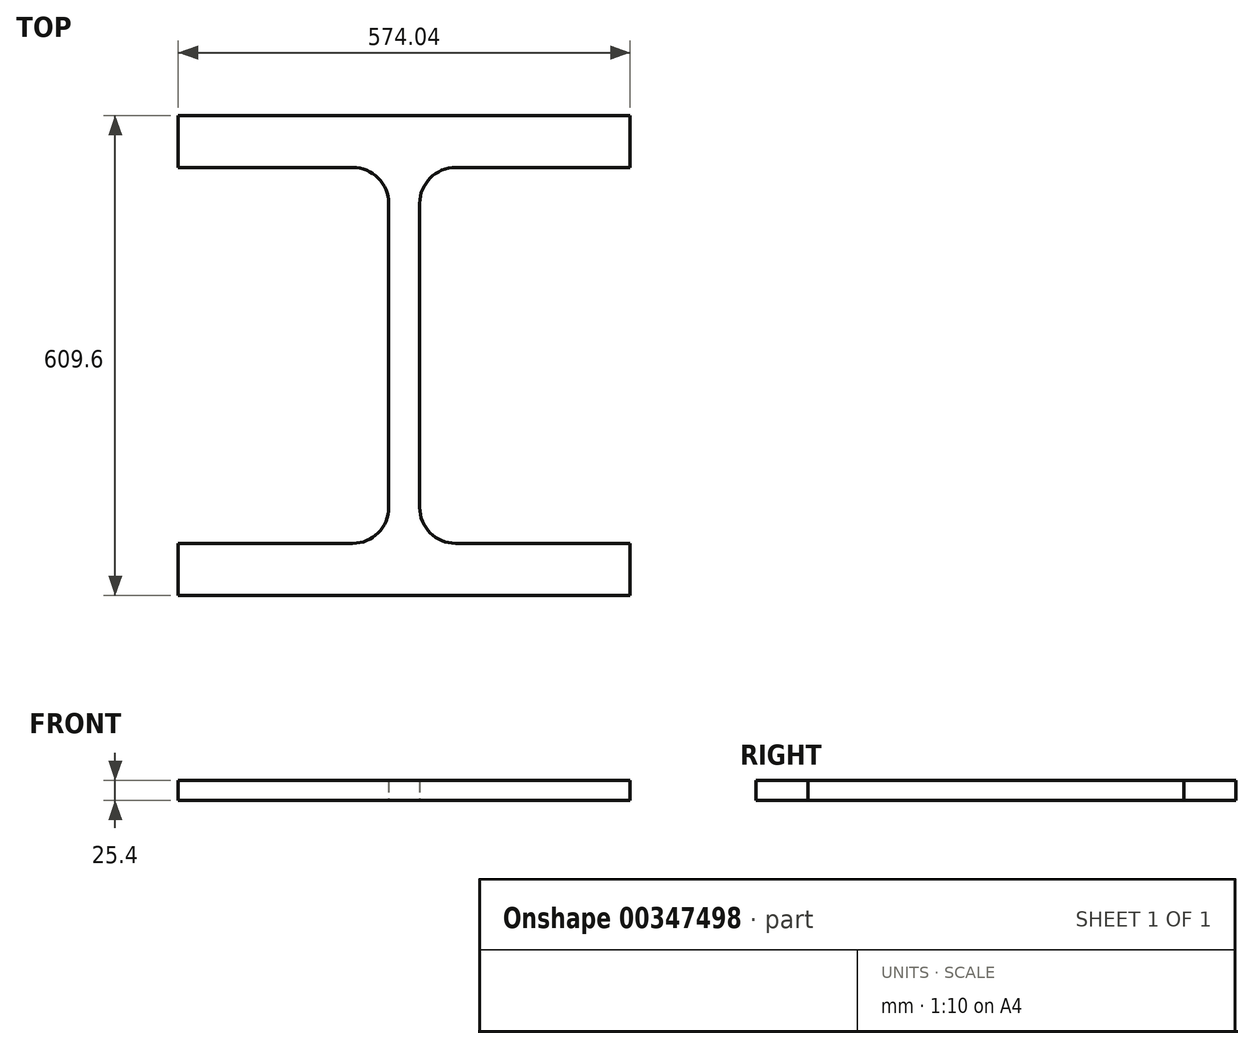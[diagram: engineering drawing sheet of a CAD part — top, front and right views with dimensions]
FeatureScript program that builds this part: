
annotation { "Feature Type Name" : "Feature", "Feature Type Description" : "" }
export const myFeature = defineFeature(function(context is Context, id is Id, definition is map)
    precondition{}
    {
        {
            var Q0;
            Q0=qCreatedBy(makeId("Top.planeOp"),FACE);
            var sketch = newSketch(context, id + "F0", { "sketchPlane" : qUnion([Q0])});
            skLineSegment(sketch, "E0", {"start": v(-308.7, -82.88) * mm, "end": v(265.35, -82.88) * mm});
            skLineSegment(sketch, "E1", {"start": v(265.35, -82.88) * mm, "end": v(265.35, -16.84) * mm});
            skLineSegment(sketch, "E2", {"start": v(265.35, -16.84) * mm, "end": v(43.73, -16.84) * mm});
            skLineSegment(sketch, "E3", {"start": v(-1.99, 28.88) * mm, "end": v(-1.99, 414.96) * mm});
            skLineSegment(sketch, "E4", {"start": v(43.73, 460.68) * mm, "end": v(265.35, 460.68) * mm});
            skLineSegment(sketch, "E5", {"start": v(265.35, 460.68) * mm, "end": v(265.35, 526.72) * mm});
            skLineSegment(sketch, "E6", {"start": v(265.35, 526.72) * mm, "end": v(-308.7, 526.72) * mm});
            skLineSegment(sketch, "E7", {"start": v(-308.7, 526.72) * mm, "end": v(-308.7, 460.68) * mm});
            skLineSegment(sketch, "E8", {"start": v(-41.36, 301.35) * mm, "end": v(-41.36, 28.88) * mm});
            skLineSegment(sketch, "E9", {"start": v(-41.36, 301.35) * mm, "end": v(-41.36, 414.96) * mm});
            skLineSegment(sketch, "E10", {"start": v(-87.08, 460.68) * mm, "end": v(-308.7, 460.68) * mm});
            skLineSegment(sketch, "E11", {"start": v(-308.7, -82.88) * mm, "end": v(-308.7, -16.84) * mm});
            skLineSegment(sketch, "E12", {"start": v(-87.08, -16.84) * mm, "end": v(-308.7, -16.84) * mm});
            skPoint(sketch, "E13.visualSharp", {"position": v(-1.99, 460.68) * mm});
            skArc(sketch, "E13.filletArc", {"start": v(43.73, 460.68) * mm, "mid": v(11.4, 447.29) * mm, "end": v(-1.99, 414.96) * mm});
            skPoint(sketch, "E14.visualSharp", {"position": v(-1.99, -16.84) * mm});
            skArc(sketch, "E14.filletArc", {"start": v(-1.99, 28.88) * mm, "mid": v(11.4, -3.45) * mm, "end": v(43.73, -16.84) * mm});
            skPoint(sketch, "E15.visualSharp", {"position": v(-41.36, -16.84) * mm});
            skArc(sketch, "E15.filletArc", {"start": v(-87.08, -16.84) * mm, "mid": v(-54.75, -3.45) * mm, "end": v(-41.36, 28.88) * mm});
            skPoint(sketch, "E16.visualSharp", {"position": v(-41.36, 460.68) * mm});
            skArc(sketch, "E16.filletArc", {"start": v(-41.36, 414.96) * mm, "mid": v(-54.75, 447.29) * mm, "end": v(-87.08, 460.68) * mm});
            skSolve(sketch);
        }
        {
            var Q0;
            Q0 = qSketchRegion(id + "F0", true);
            extrude(context, id + "F1", {"entities" : qUnion([Q0]), "depth" : 25.4 * mm});
        }
    });
